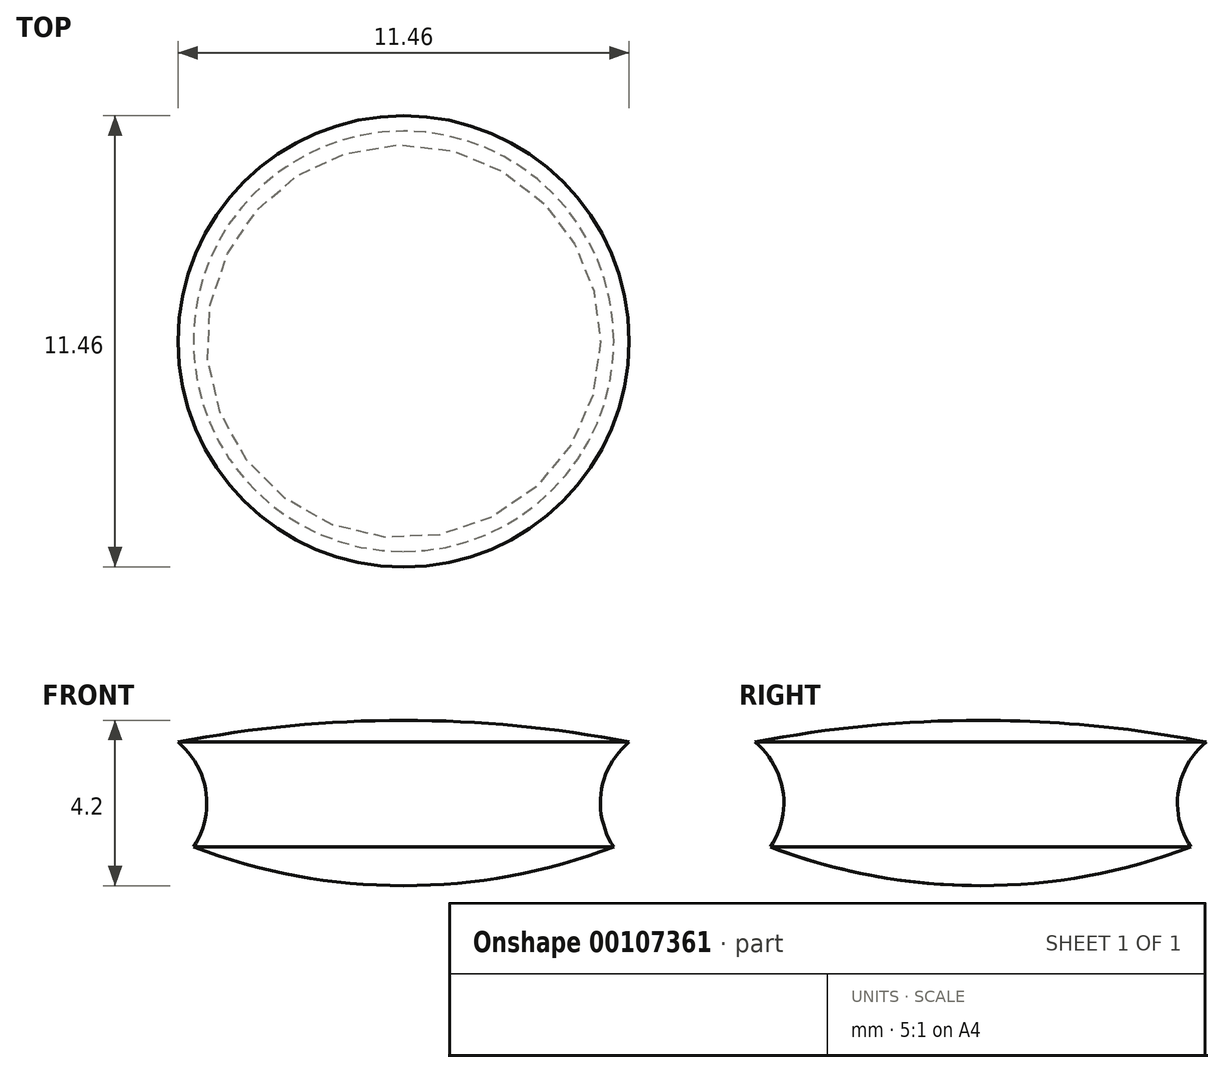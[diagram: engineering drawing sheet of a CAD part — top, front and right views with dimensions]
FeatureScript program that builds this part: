
annotation { "Feature Type Name" : "Feature", "Feature Type Description" : "" }
export const myFeature = defineFeature(function(context is Context, id is Id, definition is map)
    precondition{}
    {
        {
            var Q0;
            Q0=qCreatedBy(makeId("Right.planeOp"),FACE);
            var sketch = newSketch(context, id + "F0", { "sketchPlane" : qUnion([Q0])});
            skArc(sketch, "E0", {"start": v(-5.34, 0.98) * mm, "mid": v(-5.02, 2.4) * mm, "end": v(-5.73, 3.65) * mm});
            skArc(sketch, "E1", {"start": v(-5.34, 0.98) * mm, "mid": v(-2.72, 0.25) * mm, "end": v(0, 0) * mm});
            skArc(sketch, "E2", {"start": v(0, 4.2) * mm, "mid": v(-2.88, 4.06) * mm, "end": v(-5.73, 3.65) * mm});
            skLineSegment(sketch, "E3", {"start": v(0, 4.2) * mm, "end": v(0, 0) * mm});
            skSolve(sketch);
        }
        {
            var Q0;
            Q0=makeQuery(id+"F0.imprint","IMPRINT",FACE,{"disambiguationData":[TD([[makeQuery(id+"F0.imprint","IMPRINT",EDGE,{"derivedFrom":sQuery(id+"F0.wireOp",EDGE,"E0")}),-1.0]])]});
            var Q1;
            Q1=sQuery(id+"F0.wireOp",EDGE,"E3");
            revolve(context, id + "F1", {"entities" : qUnion([Q0]), "axis" : qUnion([Q1]), "revolveType" : RevolveType.FULL});
        }
    });
